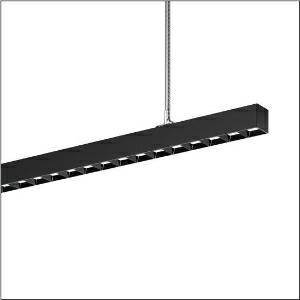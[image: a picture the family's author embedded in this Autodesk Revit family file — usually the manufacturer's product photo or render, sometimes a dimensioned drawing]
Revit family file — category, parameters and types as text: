
# Revit family: silica_r__21_51mx34dc3dbb_b9b0
name_source: partatom
category: Lighting Fixtures
units: mm (PartAtom-declared; Revit-internal decimal feet)

## family parameters
Cut with Voids When Loaded = No
Host = Face
Light Source = No
Part Type = Normal
Room Calculation Point = No
Round Connector Dimension = Use Diameter
Shared = No

## types (1)
- --- (1 x LED, 19200 lm, 129.1 W, 3000K)
    Apparent Load = 129 VA
    CIE Flux Codes = 74 94 99 56 100
    Color Rendering = 80
    Color Temperature = 3000K
    Default Elevation = 1800 mm
    Description = Silica® 21, office luminaire, primary light control with darklight reflector, of PMMA, black, light emission: direct/indirect distribution, primary light characteristic: asymmetric, installation type: suspended mounting, LED, rated luminous flux: 19.200lm, luminous efficacy: 149lm/W, light colour: 830, colour temperature: 3000K, with terminal, 3+2-pole, max. 2.5mm², mains connection: 220..240V, AC, 50/60Hz, rated input power: 129.1W, luminaire housing, of aluminium, jet black (RAL 9005), length: 3.004mm, width: 53mm, height: 53mm, protection rating (complete): IP20, insulation class (complete): insulation class I (protective earthing), certification: CE, permissible operating ambient temperature: 0..+35°C, standard: EN 50419, packaging unit: 1 piece
    Height = 53 mm
    Lamp = 1 x LED
    Lamp Light Flux = 19200 lm
    Lamp Power = 129.1 W
    Lamp count = 1
    Length = 3004 mm
    Luminous efficacy = 149 lm/W
    Manufacturer = Siteco
    ModVariant = No
    Model = 51MX34DC3DBB
    Mounting Place = Ceiling
    Mounting Type = Pendant
    Number of Poles = 1
    OnlyDefault = Yes
    Power Factor = 1
    Product Name = Silica® 21
    Product group = office luminaire | ceiling pendant
    ProductGroupID = 905
    Protection Class = Protection class I
    Protection Degree = IP 20
    RLX_Detail_Level = 1
    RlxData = <blob elided: 67333 chars, md5=b936b470>
    Socket = socket
    Standby Power = 0 W
    System Light Flux = 19200 lm
    System Power = 129 W
    Type Comments = factory setting: luminous flux: 100 % | dim-lin: 254 | 448 mA
    Type Image = l_1251718.jpg
    URL = http://relux.com
    VarID = @adj_029111
    Voltage = 0 V
    Weight = 0.00 kg
    Width = 53 mm

## geometry (parser evidence)
native form markers: Blend x4, Sweep x11
no freeform markers — native parametric forms only
